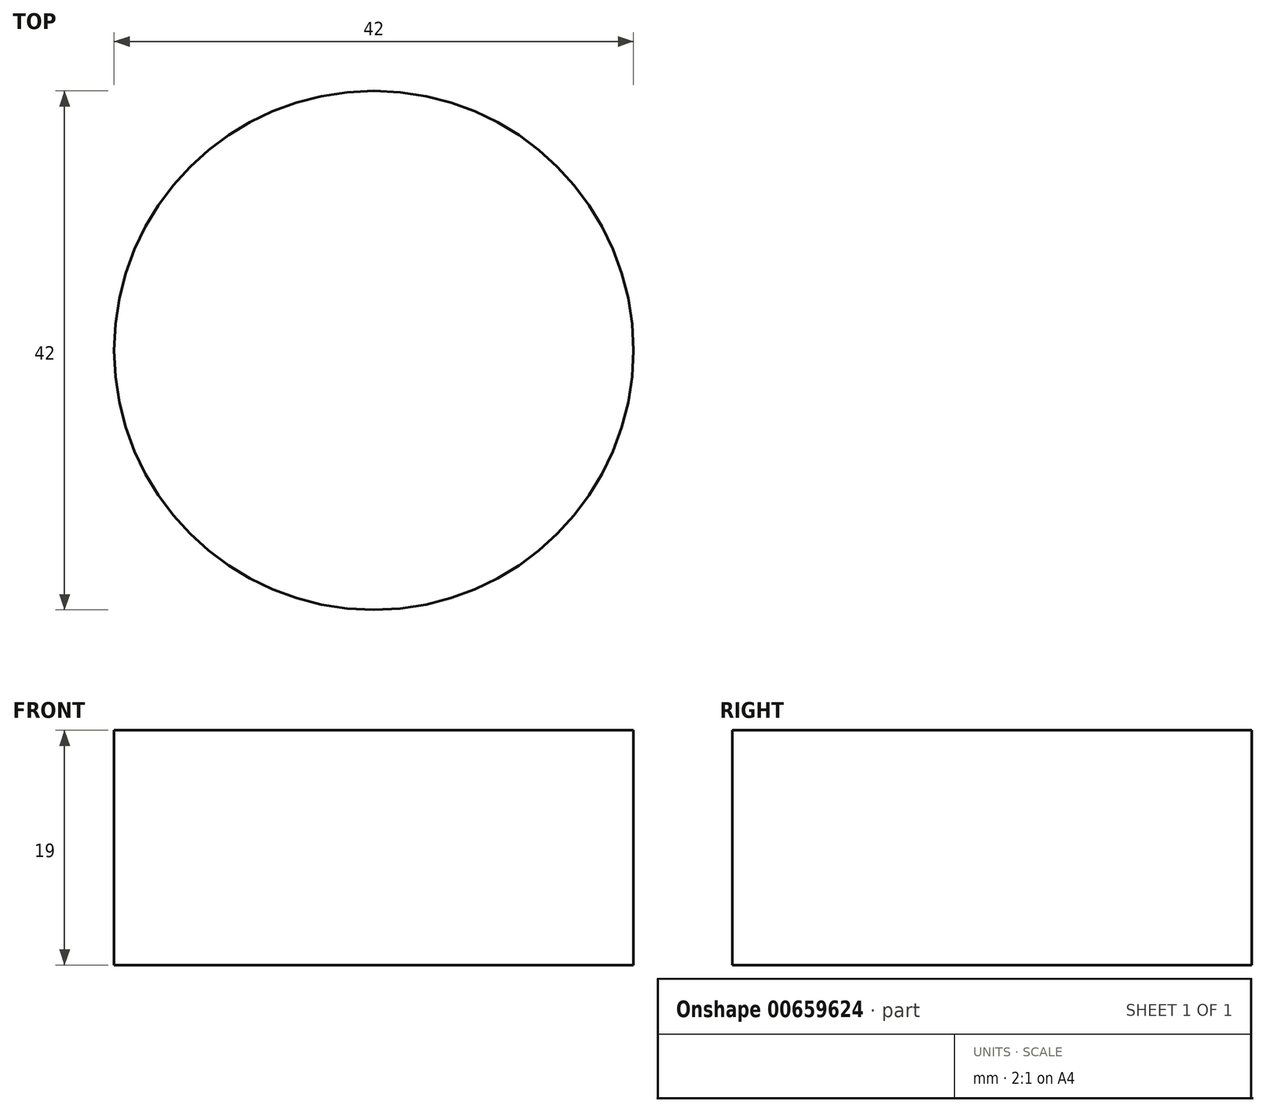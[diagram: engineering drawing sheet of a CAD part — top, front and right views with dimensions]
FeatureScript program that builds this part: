
annotation { "Feature Type Name" : "Feature", "Feature Type Description" : "" }
export const myFeature = defineFeature(function(context is Context, id is Id, definition is map)
    precondition{}
    {
        {
            var Q0;
            Q0=qCreatedBy(makeId("Top.planeOp"),FACE);
            var sketch = newSketch(context, id + "F0", { "sketchPlane" : qUnion([Q0])});
            skCircle(sketch, "E0", {"center": v(0, 0) * mm, "radius": 21 * mm});
            skSolve(sketch);
        }
        {
            var Q0;
            Q0 = qSketchRegion(id + "F0", true);
            extrude(context, id + "F1", {"entities" : qUnion([Q0]), "depth" : 19 * mm, "offsetDistance" : 25 * mm});
        }
    });
